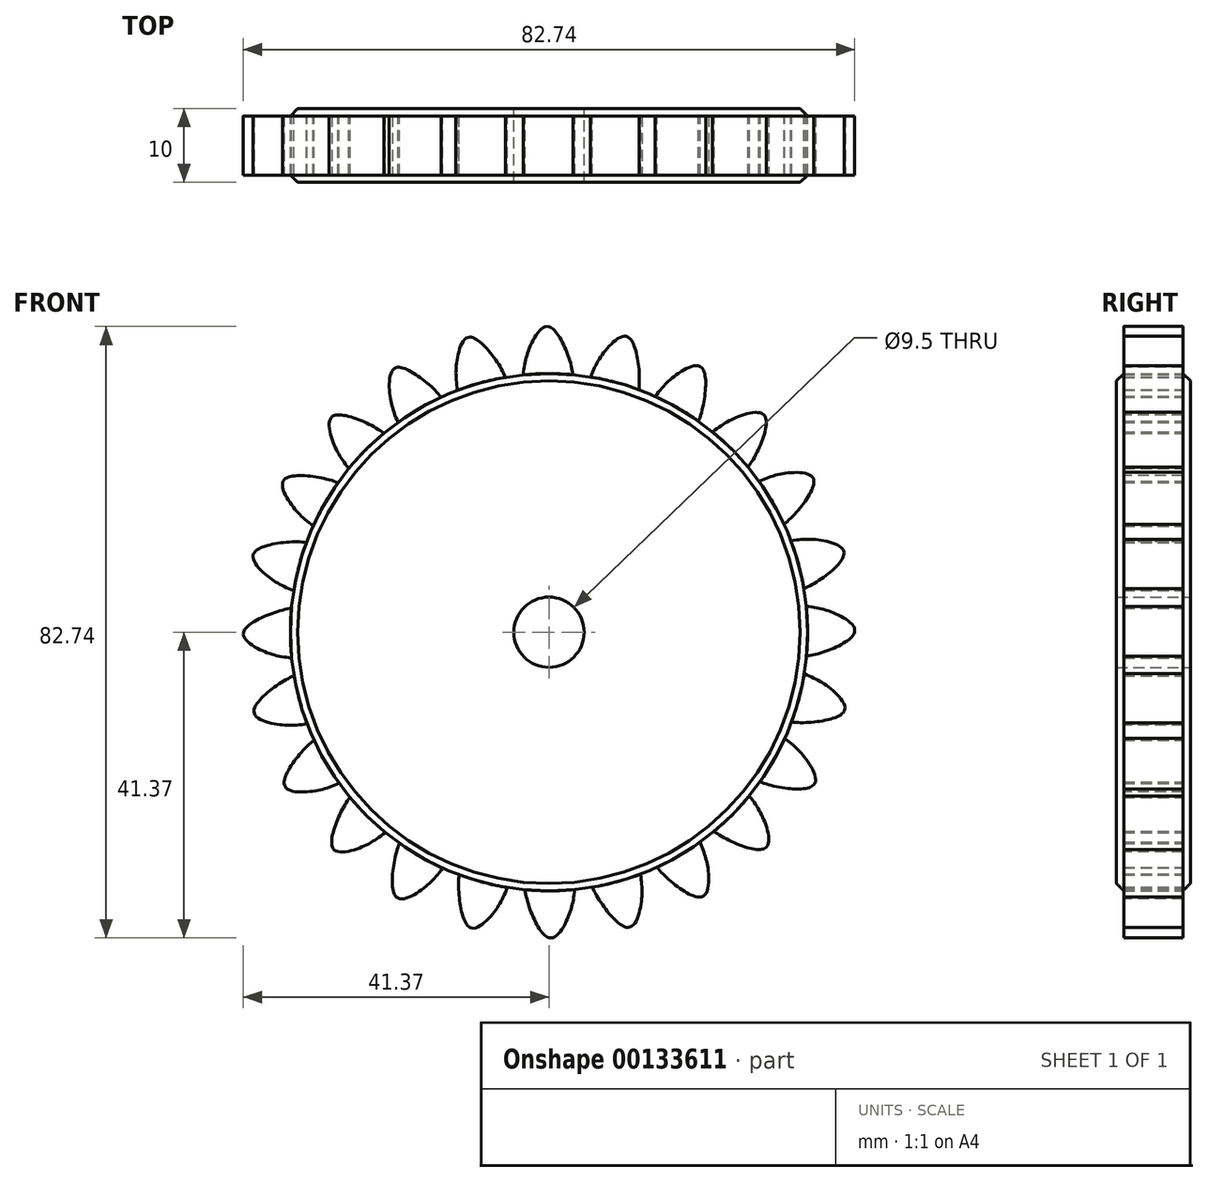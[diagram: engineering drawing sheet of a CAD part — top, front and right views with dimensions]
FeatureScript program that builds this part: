
annotation { "Feature Type Name" : "Feature", "Feature Type Description" : "" }
export const myFeature = defineFeature(function(context is Context, id is Id, definition is map)
    precondition{}
    {
        {
            var Q0;
            Q0=qCreatedBy(makeId("Front.planeOp"),FACE);
            var sketch = newSketch(context, id + "F0", { "sketchPlane" : qUnion([Q0])});
            skCircle(sketch, "E0", {"center": v(0, 0) * mm, "radius": 35 * mm});
            skCircle(sketch, "E1", {"center": v(0, 0) * mm, "radius": 4.75 * mm});
            skFitSpline(sketch, "E2", {"points": [v(-3.5, 34.82) * mm, v(-2.53, 38.71) * mm, v(0, 41.35) * mm, v(3.24, 34.85) * mm], "startDerivative": vector(2.08, 14.87) * mm, "endDerivative": vector(1.89, -15.03) * mm});
            skFitSpline(sketch, "E3.MirrorCS", {"points": [v(3.5, 34.82) * mm, v(2.53, 38.71) * mm, v(0, 41.35) * mm, v(-3.24, 34.85) * mm], "startDerivative": vector(-2.08, 14.87) * mm, "endDerivative": vector(-1.89, -15.03) * mm});
            skSolve(sketch);
        }
        {
            var Q0;
            Q0=makeQuery(id+"F0.imprint","IMPRINT",FACE,{"disambiguationData":[TD([[makeQuery(id+"F0.imprint","IMPRINT",EDGE,{"derivedFrom":sQuery(id+"F0.wireOp",EDGE,"E1")}),-1.0]])]});
            extrude(context, id + "F1", {"entities" : qUnion([Q0]), "endBound" : BoundingType.SYMMETRIC, "depth" : 10 * mm});
        }
        {
            var Q0;
            {var subQ0=sQuery(id+"F0.wireOp",EDGE,"E2");Q0=makeQuery(id+"F0.imprint","IMPRINT",FACE,{"disambiguationData":[TD([[makeQuery(id+"F0.imprint","IMPRINT",EDGE,{"derivedFrom":subQ0}),-1.0]])]});}
            extrude(context, id + "F2", {"entities" : qUnion([Q0]), "endBound" : BoundingType.SYMMETRIC, "depth" : 8 * mm});
        }
        {
            var Q0;
            Q0=makeQuery(id+"F2.opExtrude","SWEPT_BODY",BODY,{"disambiguationData":[OSD([sQuery(id+"F0.wireOp",EDGE,"E0"),sQuery(id+"F0.wireOp",EDGE,"E2"),sQuery(id+"F0.wireOp",EDGE,"E3.MirrorCS")])]});
            var Q1;
            Q1=makeQuery(id+"F1.opExtrude","SWEPT_FACE",FACE,{"disambiguationData":[OSD([sQuery(id+"F0.wireOp",EDGE,"E1")])]});
            circularPattern(context, id + "F3", {"entities" : qUnion([Q0]), "axis" : qUnion([Q1]), "angle" : 15 * degree, "instanceCount" : 30});
        }
        {
            var Q0;
            Q0=makeQuery(id+"F1.opExtrude","CAP_EDGE",EDGE,{"disambiguationData":[OSD([sQuery(id+"F0.wireOp",EDGE,"E0")])],"isStart":false});
            chamfer(context, id + "F4", {"entities" : qUnion([Q0]), "width" : 1 * mm, "tangentPropagation" : true});
        }
        {
            var Q0;
            Q0=makeQuery(id+"F1.opExtrude","CAP_EDGE",EDGE,{"disambiguationData":[OSD([sQuery(id+"F0.wireOp",EDGE,"E0")])],"isStart":true});
            chamfer(context, id + "F5", {"entities" : qUnion([Q0]), "width" : 1 * mm, "tangentPropagation" : true});
        }
    });
